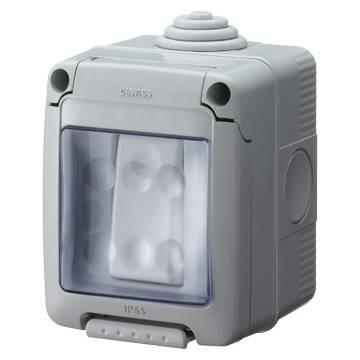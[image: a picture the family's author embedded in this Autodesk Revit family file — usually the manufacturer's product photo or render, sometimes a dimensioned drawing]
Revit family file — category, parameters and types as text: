
# Revit family: Domotics-DomesticRanges-GEWISS-27COMBI_SYSTEM-IP55_COMMAND_1M
name_source: partatom
category: Apparecchi elettrici
revit_build: Autodesk Revit 2016 (Build: 20161004_0715(x64)
units: mm (PartAtom-declared; Revit-internal decimal feet)

## family parameters
Condiviso = Sì
Host = Superficie
Mantenere orientamento annotazione = Sì
Numero OmniClass = 23.80.50.11.14
Punto di calcolo locali = No
Quota connettore circolare = Usa diametro
Taglio con vuoti quando caricato = Sì
Tipo di parte = Normale
Titolo OmniClass = Switches

## types (1)
- Domotics-DomesticRanges-GEWISS-27COMBI_SYSTEM-IP55_COMMAND_1M
    Catalogue = DOMOTICS
    Catalogue Range = 27COMBI
    Classificazione = Altro
    Colour = Grey RAL 7035
    Description: = Push-button 1P NO 10A
    Descrizione = 10A 1P PUSH-BUTTON IP55
    Door colour: = Transparent
    Door type = With membrane
    EAN code = 8011564095441
    Electrocod = 0130
    Glow Wire Test = 650°C
    IDF = 65811628-2d58-4a32-8d4c-6142d7f9f502
    IDT = 2d0f21d1-8ef9-4ef1-9a1b-35e0feede76f
    IP degree = IP55
    Immagine tipo = GW27835.jpg
    Installation temperature = -25 +60 °C
    Insulation class = II
    Lid screws = Stainless steel
    Modello = GW27835
    N. holes Ã˜ 23 with cable gland = 1
    No. knockout holes Ã˜23 = 3 on sides / 1 on the bottom
    Offset = 0 mm  [stored 0 ft]
    Outer dim. LxHxD (mm) = 66x82x65
    Produttore = GEWISS S.p.A.
    Prospetto di default = 1219 mm
    SEO = Enclosure
    Standard; = EN 60669-1
    Technical sheet = https://www.gewiss.com
    Thermo-pressure with ball = 70
    Tipo simbolo = SIMBOLO PULSANTI : PULSANTE
    Torque screws tightening = 0,8NM
    Type = Push-button 1P NO 10A
    Type of knockout holes = Removable with tool
    URL = https://www.gewiss.com
    Version file RFA = 19.4
    Vetrino luminoso = Sì
    Voltage = 230V ac
    Voltage: = 250 V ac

note: source unit labels omitted for Thermo-pressure with ball — the stored unit's dimension contradicts the parameter name (converter mislabeling)

note: [stored X ft] marks values corroborated as IEEE doubles in the binary element streams (Revit-internal decimal feet)

## geometry (parser evidence)
native form markers: Sweep x4
no freeform markers — native parametric forms only
